# Revit family: P190780JX-156c_JXW9036HP_StainlessSteel_JA_Cooking_Ventilation
name_source: partatom
category: Specialty Equipment
units: mm (PartAtom-declared; Revit-internal decimal feet)

## family parameters
Always vertical = Yes
Cut with Voids When Loaded = No
Enable Cutting in Views = No
Maintain Annotation Orientation = No
Part Type = Normal
Room Calculation Point = No
Round Connector Dimension = Use Diameter
Shared = No
Work Plane-Based = No

## types (1)
- JXW9036HP
    Accent Material = ARCAT - Metal - Steel - Gray
    Amps = 0 A
    Body Material = ARCAT - Metal - Steel - Stainless
    Default Elevation = 0"
    Depth = 25"
    Description = Pro-Style® 36"Professional Wall-Mount Hood
Hotte murale professionnelle, 36 po
    Family Name = COMMERCIAL & LINER HOODS - 36"
    Feature 1 = Velocity Blower
Ventilateur à grande vitesse
    Feature 2 = 10-Inch Round Exterior Venting
Ventilation extérieure ronde de 10 po
    Feature 3 = Radiant Until Ready
Radiant jusqu’à ce qu’il soit prêt
    Height = 19 3/8"
    Installation-Fabrication = http://access.whirlpool.com Instruction&sku=JXW9036HP&language=EN
http://access.whirlpool.com Instruction&sku=JXW9036HP&language=EN
    Knob Material = ARCAT - Metal - Steel - Black
    Manufacturer = Jenn Air
    Model = JXW9036HP
    Vent Material = ARCAT - Metal - Steel - Gray
    Voltage = 0 V
    Width = 36"

## geometry (parser evidence)
native form markers: Sweep x5
no freeform markers — native parametric forms only
